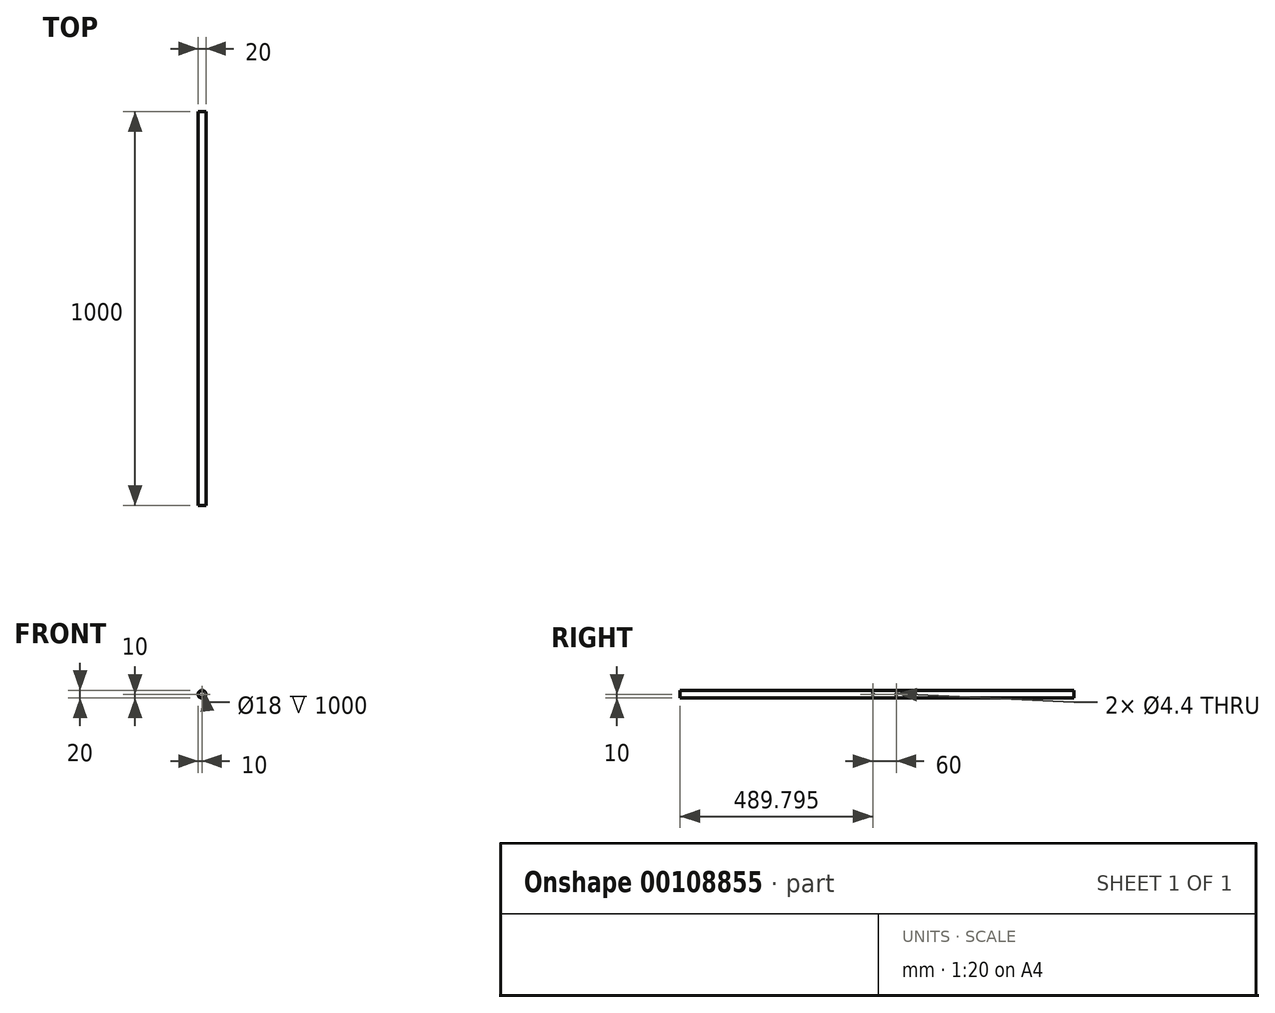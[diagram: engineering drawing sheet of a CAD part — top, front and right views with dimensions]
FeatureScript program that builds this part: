
annotation { "Feature Type Name" : "Feature", "Feature Type Description" : "" }
export const myFeature = defineFeature(function(context is Context, id is Id, definition is map)
    precondition{}
    {
        {
            var Q0;
            Q0=qCreatedBy(makeId("Front.planeOp"),FACE);
            var sketch = newSketch(context, id + "F0", { "sketchPlane" : qUnion([Q0])});
            skCircle(sketch, "E0", {"center": v(0, 0) * mm, "radius": 10 * mm});
            skCircle(sketch, "E1", {"center": v(0, 0) * mm, "radius": 9 * mm});
            skSolve(sketch);
        }
        {
            var Q0;
            Q0=makeQuery(id+"F0.imprint","IMPRINT",FACE,{"disambiguationData":[TD([[makeQuery(id+"F0.imprint","IMPRINT",EDGE,{"derivedFrom":sQuery(id+"F0.wireOp",EDGE,"E0")}),1.0]])]});
            var Q1;
            Q1=sQuery(id+"F0.wireOp",EDGE,"E1");
            var Q2;
            Q2=sQuery(id+"F0.wireOp",EDGE,"E0");
            extrude(context, id + "F1", {"entities" : qUnion([Q0]), "surfaceEntities" : qUnion([Q1, Q2]), "depth" : 1000 * mm});
        }
        {
            var Q0;
            Q0=qCreatedBy(makeId("Right.planeOp"),FACE);
            var sketch = newSketch(context, id + "F2", { "sketchPlane" : qUnion([Q0])});
            skLineSegment(sketch, "E2", {"start": v(47.64, 0) * mm, "end": v(-1009.74, 0) * mm, "construction": true});
            skLineSegment(sketch, "E3", {"start": v(-980.2, -16.32) * mm, "end": v(-980.2, 44.8) * mm, "construction": true});
            skLineSegment(sketch, "E4", {"start": v(0, -10.7) * mm, "end": v(0, 37.1) * mm, "construction": true});
            skLineSegment(sketch, "E5", {"start": v(-510.2, 76.76) * mm, "end": v(-510.2, -85.46) * mm, "construction": true});
            skLineSegment(sketch, "E6", {"start": v(-450.2, 80.42) * mm, "end": v(-450.2, -107.42) * mm, "construction": true});
            skPoint(sketch, "E7", {"position": v(-510.2, 0) * mm});
            skPoint(sketch, "E8", {"position": v(-450.2, 0) * mm});
            skSolve(sketch);
        }
        {
            var Q0;
            Q0=sQuery(id+"F2.wireOp",VERTEX,"E7");
            var Q1;
            Q1=sQuery(id+"F2.wireOp",VERTEX,"E8");
            var Q2;
            Q2=makeQuery(id+"F1.opExtrude","SWEPT_BODY",BODY,{"disambiguationData":[OSD([sQuery(id+"F0.wireOp",EDGE,"E0"),sQuery(id+"F0.wireOp",EDGE,"E1")])]});
            hole(context, id + "F3", {"style" : HoleStyle.SIMPLE, "endStyle" : HoleEndStyle.THROUGH, "oppositeDirection" : true, "standardTappedOrClearance" : lookupTablePath({ "standard" : "ISO", "fit" : "Normal", "size" : "M4", "type" : "Clearance" }), "standardBlindInLast" : lookupTablePath({ "fit" : "Standard", "standard" : "ISO", "size" : "M4", "type" : "Clearance" }), "holeDiameter" : 4.4 * mm, "startFromSketch" : true, "locations" : qUnion([Q0, Q1]), "scope" : qUnion([Q2]), "isTappedThrough" : true});
        }
    });
